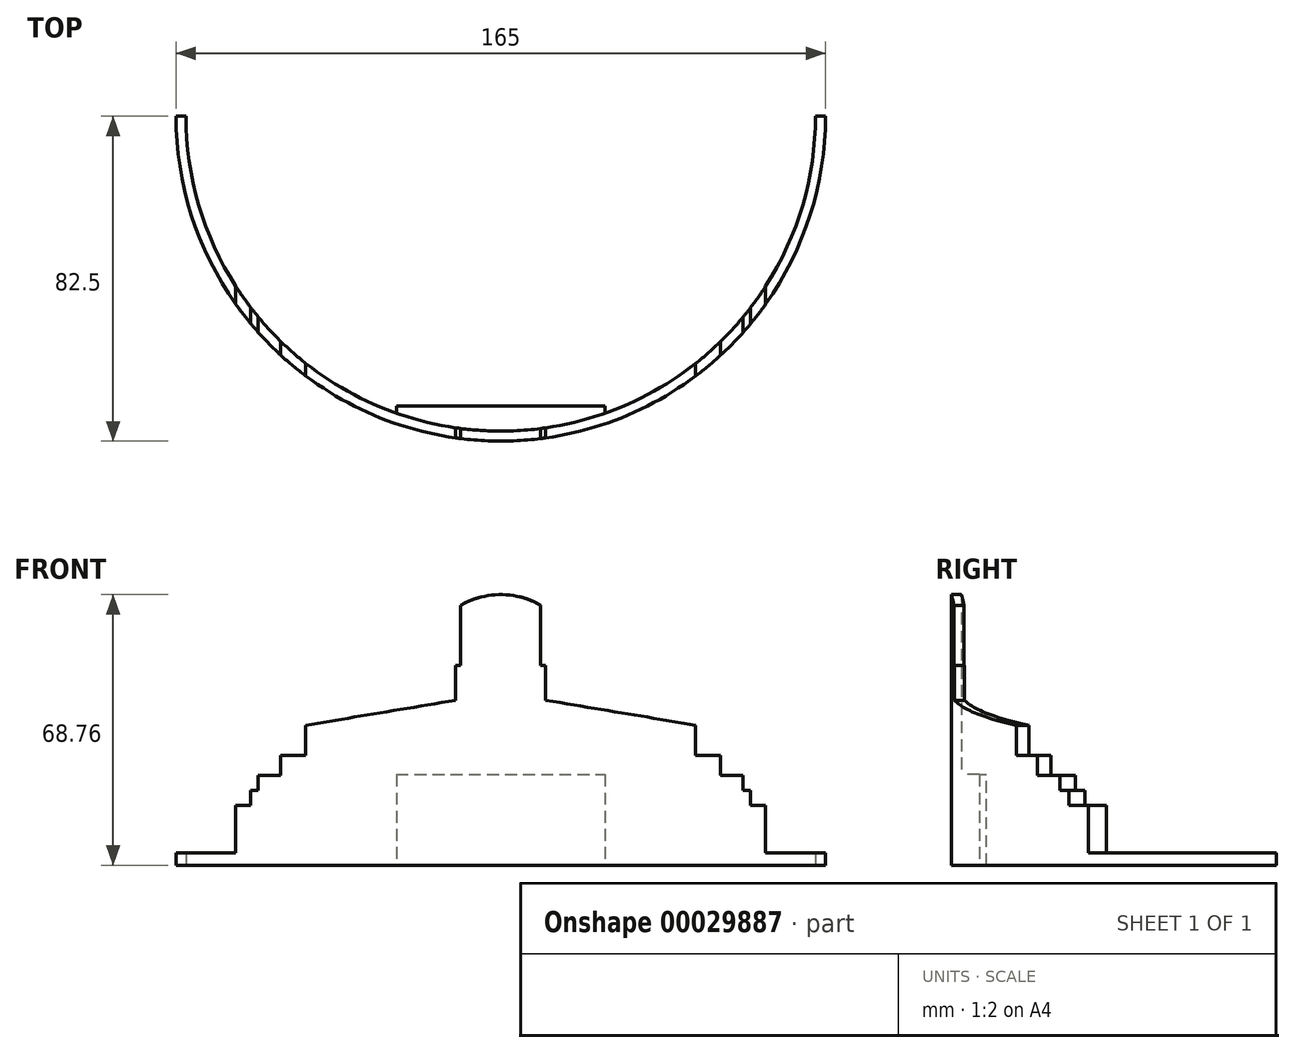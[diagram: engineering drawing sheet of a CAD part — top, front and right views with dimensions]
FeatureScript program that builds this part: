
annotation { "Feature Type Name" : "Feature", "Feature Type Description" : "" }
export const myFeature = defineFeature(function(context is Context, id is Id, definition is map)
    precondition{}
    {
        {
            var Q0;
            Q0=qCreatedBy(makeId("Front.planeOp"),FACE);
            var sketch = newSketch(context, id + "F0", { "sketchPlane" : qUnion([Q0])});
            skLineSegment(sketch, "E0", {"start": v(-67.31, 0) * mm, "end": v(67.31, 0) * mm});
            skLineSegment(sketch, "E1", {"start": v(67.31, 0) * mm, "end": v(67.31, 15.24) * mm});
            skLineSegment(sketch, "E2", {"start": v(67.31, 15.24) * mm, "end": v(63.5, 15.24) * mm});
            skLineSegment(sketch, "E3", {"start": v(63.5, 15.24) * mm, "end": v(63.5, 19.05) * mm});
            skLineSegment(sketch, "E4", {"start": v(63.5, 19.05) * mm, "end": v(61.6, 19.05) * mm});
            skLineSegment(sketch, "E5", {"start": v(61.6, 19.05) * mm, "end": v(61.6, 22.86) * mm});
            skLineSegment(sketch, "E6", {"start": v(61.6, 22.86) * mm, "end": v(55.88, 22.86) * mm});
            skLineSegment(sketch, "E7", {"start": v(55.88, 22.86) * mm, "end": v(55.88, 27.94) * mm});
            skLineSegment(sketch, "E8", {"start": v(55.88, 27.94) * mm, "end": v(49.53, 27.94) * mm});
            skLineSegment(sketch, "E9", {"start": v(49.53, 27.94) * mm, "end": v(49.53, 35.56) * mm});
            skLineSegment(sketch, "E10", {"start": v(49.53, 35.56) * mm, "end": v(11.43, 41.91) * mm});
            skLineSegment(sketch, "E11", {"start": v(11.43, 41.91) * mm, "end": v(11.43, 50.8) * mm});
            skLineSegment(sketch, "E12", {"start": v(11.43, 50.8) * mm, "end": v(10.16, 50.8) * mm});
            skLineSegment(sketch, "E13", {"start": v(10.16, 50.8) * mm, "end": v(10.16, 66.04) * mm});
            skLineSegment(sketch, "E14", {"start": v(10.16, 66.04) * mm, "end": v(0, 66.04) * mm, "construction": true});
            skLineSegment(sketch, "E15", {"start": v(0, 66.04) * mm, "end": v(0, 0) * mm, "construction": true});
            skLineSegment(sketch, "E16.MirrorCS", {"start": v(-10.16, 66.04) * mm, "end": v(0, 66.04) * mm, "construction": true});
            skLineSegment(sketch, "E17.MirrorCS", {"start": v(-10.16, 50.8) * mm, "end": v(-10.16, 66.04) * mm});
            skLineSegment(sketch, "E18.MirrorCS", {"start": v(-11.43, 41.91) * mm, "end": v(-11.43, 50.8) * mm});
            skLineSegment(sketch, "E19.MirrorCS", {"start": v(-49.53, 35.56) * mm, "end": v(-11.43, 41.91) * mm});
            skLineSegment(sketch, "E20.MirrorCS", {"start": v(-49.53, 27.94) * mm, "end": v(-49.53, 35.56) * mm});
            skLineSegment(sketch, "E21.MirrorCS", {"start": v(-55.88, 27.94) * mm, "end": v(-49.53, 27.94) * mm});
            skLineSegment(sketch, "E22.MirrorCS", {"start": v(-55.88, 22.86) * mm, "end": v(-55.88, 27.94) * mm});
            skLineSegment(sketch, "E23.MirrorCS", {"start": v(-61.6, 22.86) * mm, "end": v(-55.88, 22.86) * mm});
            skLineSegment(sketch, "E24.MirrorCS", {"start": v(-61.6, 19.05) * mm, "end": v(-61.6, 22.86) * mm});
            skLineSegment(sketch, "E25.MirrorCS", {"start": v(-63.5, 15.24) * mm, "end": v(-63.5, 19.05) * mm});
            skLineSegment(sketch, "E26.MirrorCS", {"start": v(-67.31, 15.24) * mm, "end": v(-63.5, 15.24) * mm});
            skLineSegment(sketch, "E27.MirrorCS", {"start": v(-67.31, 0) * mm, "end": v(-67.31, 15.24) * mm});
            skLineSegment(sketch, "E28", {"start": v(-63.5, 19.05) * mm, "end": v(-61.6, 19.05) * mm});
            skLineSegment(sketch, "E29", {"start": v(-10.16, 50.8) * mm, "end": v(-11.43, 50.8) * mm});
            skArc(sketch, "E30", {"start": v(10.16, 66.04) * mm, "mid": v(0, 68.76) * mm, "end": v(-10.16, 66.04) * mm});
            skSolve(sketch);
        }
        {
            var Q0;
            Q0=qCreatedBy(makeId("Top.planeOp"),FACE);
            var sketch = newSketch(context, id + "F1", { "sketchPlane" : qUnion([Q0])});
            skArc(sketch, "E31", {"start": v(-81.06, 97.85) * mm, "mid": v(0, 0) * mm, "end": v(81.06, 97.85) * mm});
            skArc(sketch, "E32.0", {"start": v(-78.56, 97.38) * mm, "mid": v(0, 2.54) * mm, "end": v(78.56, 97.38) * mm});
            skLineSegment(sketch, "E33", {"start": v(-78.56, 97.38) * mm, "end": v(-81.06, 97.85) * mm});
            skLineSegment(sketch, "E34", {"start": v(81.06, 97.85) * mm, "end": v(78.56, 97.38) * mm});
            skSolve(sketch);
        }
        {
            var Q0;
            Q0 = qSketchRegion(id + "F1", true);
            extrude(context, id + "F2", {"entities" : qUnion([Q0]), "depth" : 76.2 * mm});
        }
        {
            var Q0;
            Q0 = qSketchRegion(id + "F0", true);
            extrude(context, id + "F3", {"entities" : qUnion([Q0]), "operationType" : NewBodyOperationType.INTERSECT, "oppositeDirection" : true, "depth" : 48.53 * mm});
        }
        {
            var Q0;
            Q0=qCreatedBy(makeId("Front.planeOp"),FACE);
            cPlane(context, id + "F4", {"entities" : qUnion([Q0]), "cplaneType" : CPlaneType.OFFSET, "offset" : 8.9 * mm, "oppositeDirection" : true, "width" : 152.4 * mm, "height" : 152.4 * mm});
        }
        {
            var Q0;
            Q0=qCreatedBy(id+"F4.planeOp",FACE);
            var sketch = newSketch(context, id + "F5", { "sketchPlane" : qUnion([Q0])});
            skLineSegment(sketch, "E35.bottom", {"start": v(-26.5, 0) * mm, "end": v(26.5, 0) * mm});
            skLineSegment(sketch, "E35.top", {"start": v(-26.5, 23) * mm, "end": v(26.5, 23) * mm});
            skLineSegment(sketch, "E35.left", {"start": v(-26.5, 0) * mm, "end": v(-26.5, 23) * mm});
            skLineSegment(sketch, "E35.right", {"start": v(26.5, 0) * mm, "end": v(26.5, 23) * mm});
            skSolve(sketch);
        }
        {
            var Q0;
            Q0 = qSketchRegion(id + "F5", true);
            extrude(context, id + "F6", {"entities" : qUnion([Q0]), "operationType" : NewBodyOperationType.ADD, "endBound" : BoundingType.UP_TO_NEXT, "depth" : 25.4 * mm});
        }
        {
            var Q0;
            Q0=qCreatedBy(makeId("Top.planeOp"),FACE);
            var sketch = newSketch(context, id + "F7", { "sketchPlane" : qUnion([Q0])});
            skArc(sketch, "E36.0", {"start": v(-67.31, 34.8) * mm, "mid": v(0, 0) * mm, "end": v(67.31, 34.8) * mm, "construction": true});
            skArc(sketch, "E37", {"start": v(-67.31, 34.8) * mm, "mid": v(-78.61, 57.47) * mm, "end": v(-82.5, 82.5) * mm});
            skArc(sketch, "E38.0", {"start": v(-67.31, 39.34) * mm, "mid": v(-49.6, 19.79) * mm, "end": v(-26.5, 7.06) * mm, "construction": true});
            skArc(sketch, "E39", {"start": v(-67.31, 39.34) * mm, "mid": v(-76.73, 60.01) * mm, "end": v(-79.96, 82.5) * mm});
            skLineSegment(sketch, "E40", {"start": v(-82.5, 82.5) * mm, "end": v(-79.96, 82.5) * mm});
            skLineSegment(sketch, "E41", {"start": v(0, 82.5) * mm, "end": v(0, 0) * mm, "construction": true});
            skLineSegment(sketch, "E42.0", {"start": v(-67.31, 39.34) * mm, "end": v(-67.31, 34.8) * mm});
            skLineSegment(sketch, "E43.MirrorCS", {"start": v(67.31, 39.34) * mm, "end": v(67.31, 34.8) * mm});
            skArc(sketch, "E44.MirrorCS", {"start": v(67.31, 34.8) * mm, "mid": v(78.61, 57.47) * mm, "end": v(82.5, 82.5) * mm});
            skArc(sketch, "E45.MirrorCS", {"start": v(67.31, 39.34) * mm, "mid": v(76.73, 60.01) * mm, "end": v(79.96, 82.5) * mm});
            skLineSegment(sketch, "E46.MirrorCS", {"start": v(82.5, 82.5) * mm, "end": v(79.96, 82.5) * mm});
            skSolve(sketch);
        }
        {
            var Q0;
            Q0 = qSketchRegion(id + "F7", true);
            extrude(context, id + "F8", {"entities" : qUnion([Q0]), "operationType" : NewBodyOperationType.ADD, "depth" : 3.17 * mm});
        }
    });
